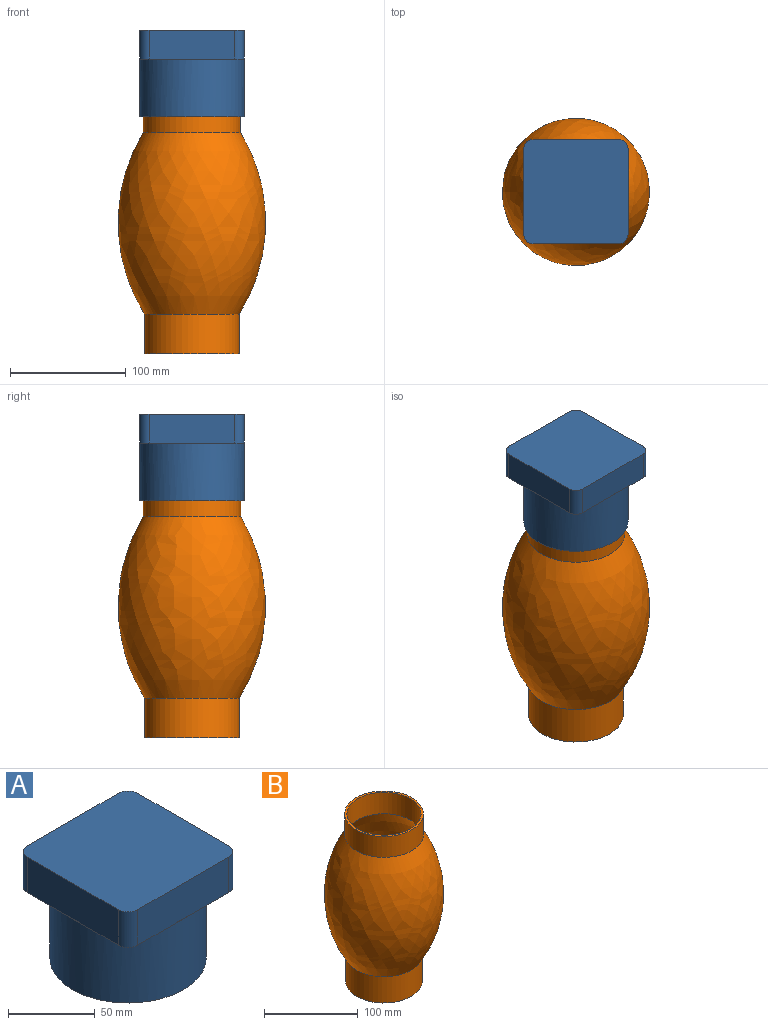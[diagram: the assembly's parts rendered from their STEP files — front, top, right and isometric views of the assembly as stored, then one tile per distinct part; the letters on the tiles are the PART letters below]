
ASSEMBLY  parts=2 mates=1
PART A: 29 faces, bbox 90x90x75 mm
  f0: cylinder r=45mm len=90mm, axis (0,0,-1), area 14137.2mm2, adj f1,f2,f3,f4,f10
  f1: plane 45x45mm, normal (0,0,-1), area 420.8mm2, adj f0,f5,f6,f21
  f2: plane 45x45mm, normal (0,0,-1), area 420.8mm2, adj f0,f6,f7,f22
  f3: plane 45x45mm, normal (0,0,-1), area 420.8mm2, adj f0,f7,f8,f23
  f4: plane 45x45mm, normal (0,0,-1), area 420.8mm2, adj f0,f5,f8,f24
  f5: plane 74x25mm, normal (1,0,0), area 1850mm2, adj f1,f4,f9,f21,f24
  f6: plane 74x25mm, normal (0,1,0), area 1850mm2, adj f1,f2,f9,f21,f22
  f7: plane 74x25mm, normal (-1,0,0), area 1850mm2, adj f2,f3,f9,f22,f23
  f8: plane 74x25mm, normal (0,-1,0), area 1850mm2, adj f3,f4,f9,f23,f24
  f9: plane 90x90mm, normal (0,0,1), area 8045.1mm2, adj f5,f6,f7,f8,f21,f22,f23,f24
  f10: plane 90x90mm, normal (0,0,-1), area 687.2mm2, adj f0,f11
  f11: cylinder r=42.5mm len=85mm, axis (0,0,-1), area 14019.4mm2, adj f10,f12,f13,f14,f15
  f12: plane 42.5x42.5mm, normal (0,0,1), area 370.2mm2, adj f11,f16,f17,f28
  f13: plane 42.5x42.5mm, normal (0,0,1), area 370.2mm2, adj f11,f17,f18,f25
  f14: plane 42.5x42.5mm, normal (0,0,1), area 370.2mm2, adj f11,f18,f19,f26
  f15: plane 42.5x42.5mm, normal (0,0,1), area 370.2mm2, adj f11,f16,f19,f27
  f16: plane 67x20mm, normal (-1,0,0), area 1340mm2, adj f12,f15,f20,f27,f28
  f17: plane 67x20mm, normal (0,-1,0), area 1340mm2, adj f12,f13,f20,f25,f28
  f18: plane 67x20mm, normal (1,0,0), area 1340mm2, adj f13,f14,f20,f25,f26
  f19: plane 67x20mm, normal (0,1,0), area 1340mm2, adj f14,f15,f20,f26,f27
  f20: plane 85x85mm, normal (0,0,-1), area 7155.5mm2, adj f16,f17,f18,f19,f25,f26,f27,f28
  f21: cylinder r=8mm len=25mm, axis (0,0,1), area 314.2mm2, adj f1,f5,f6,f9
  f22: cylinder r=8mm len=25mm, axis (0,0,-1), area 314.2mm2, adj f2,f6,f7,f9
  f23: cylinder r=8mm len=25mm, axis (0,0,1), area 314.2mm2, adj f3,f7,f8,f9
  f24: cylinder r=8mm len=25mm, axis (0,0,-1), area 314.2mm2, adj f4,f5,f8,f9
  f25: cylinder r=9mm len=20mm, axis (0,0,1), area 282.7mm2, adj f13,f17,f18,f20
  f26: cylinder r=9mm len=20mm, axis (0,0,-1), area 282.7mm2, adj f14,f18,f19,f20
  f27: cylinder r=9mm len=20mm, axis (0,0,1), area 282.7mm2, adj f15,f16,f19,f20
  f28: cylinder r=9mm len=20mm, axis (0,0,-1), area 282.7mm2, adj f12,f16,f17,f20
PART B: 9 faces, bbox 127.3x127.3x218.2 mm
  f0: plane 81.57x81.57mm, normal (0,0,-1), area 5225.2mm2, adj f1
  f1: cylinder r=40.78mm len=81.57mm, axis (0,0,-1), area 8775.1mm2, adj f0,f2
  f2: revolved ~156.74x127.27mm, area 58217.4mm2, adj f1,f3
  f3: cylinder r=42mm len=84mm, axis (0,0,-1), area 7170.4mm2, adj f2,f4
  f4: plane 84x84mm, normal (0,0,1), area 640.1mm2, adj f3,f8
  f5: plane 76.57x76.57mm, normal (0,0,1), area 4604.2mm2, adj f6
  f6: cylinder r=38.28mm len=76.57mm, axis (0,0,-1), area 7809.9mm2, adj f5,f7
  f7: revolved ~155.32x122.27mm, area 55168mm2, adj f6,f8
  f8: cylinder r=39.5mm len=79mm, axis (0,0,-1), area 6917.8mm2, adj f4,f7
PLACE A t=(-1.78,-4.34,139.2)mm
PLACE B t=(-1.78,-4.34,23.23)mm
MATE fastened A.f0 <-> B.f1  axis (0,0,-1) through (-1.78,-4.34,114.2)mm
